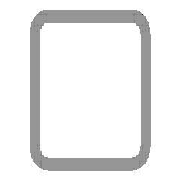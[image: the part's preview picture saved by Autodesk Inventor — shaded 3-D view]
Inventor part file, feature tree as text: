
AUTODESK INVENTOR PART (.ipt)
format: ipt  version: 2025 (Build 290162010, 162A)  size: 133,120 bytes
history: native  units: mm (DEFAULTED — no unit token found)
features: other x4, sketch x1, plane x1
ambient origin geometry x8: Origin, YZ Plane, XZ Plane, XY Plane, X Axis, Y Axis, Z Axis, Center Point
bodies: Solid1 (feature_tree), Body (feature_tree)
feature tree (6):
  parser-record x1  (decoder bookkeeping rows leaked as tree rows — omitted from the tree; the rows remain in map.json)
  other  "Driven Length"
  other  "Start Plane"
  other  "End Plane"
  sketch  "Sketch3"  dims[d3=580.0mm d4=0.0mm d7=6.0mm d9=80.0mm d11=80.0mm d12=3.0mm d13=40.0mm d14=620.0mm d15=40.0mm d16=40.0mm d17=90.0deg d18=580.0mm]
  plane  "Work Plane3"
